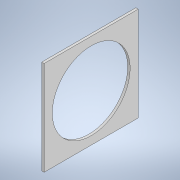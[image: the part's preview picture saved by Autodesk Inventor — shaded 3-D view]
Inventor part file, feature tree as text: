
AUTODESK INVENTOR PART (.ipt)
format: ipt  version: 2022 (Build 260153000, 153)  size: 101,376 bytes
history: native  units: mm
features: extrude x1, sketch x1
ambient origin geometry x8: Origin, YZ Plane, XZ Plane, XY Plane, X Axis, Y Axis, Z Axis, Center Point
bodies: Solid1 (feature_tree)
feature tree (2):
  extrude  "Extrusion1"  Depth=38.75mm
  sketch  "Sketch1"  dims[d0=38.75mm d1=38.75mm d2=32.0mm d3=1.0mm d4=0.0mm]
